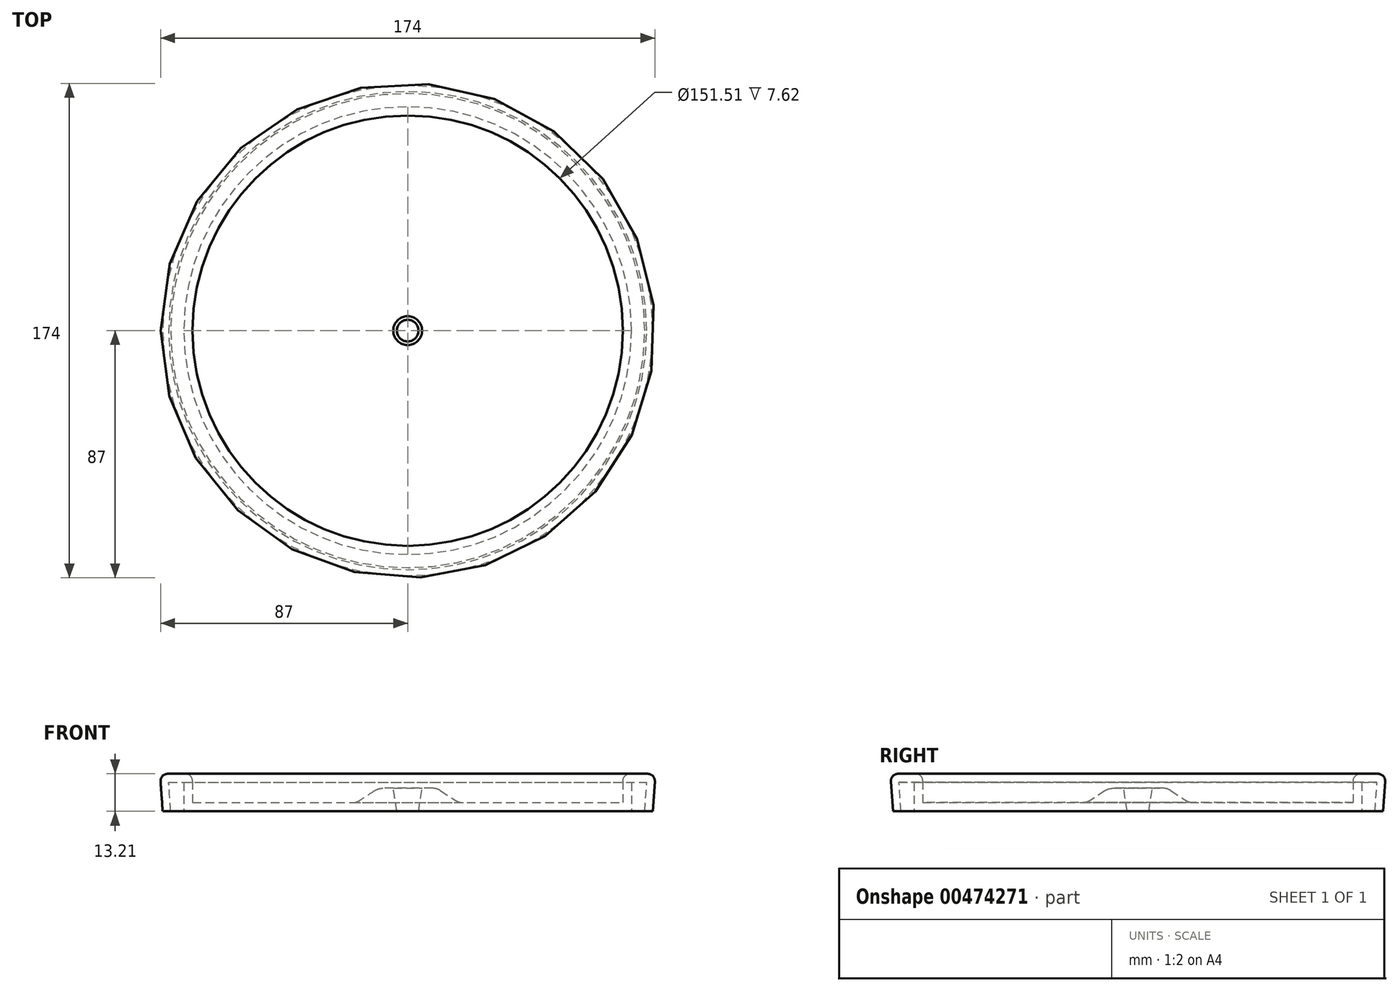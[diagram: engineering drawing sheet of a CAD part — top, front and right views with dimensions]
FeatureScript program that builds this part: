
annotation { "Feature Type Name" : "Feature", "Feature Type Description" : "" }
export const myFeature = defineFeature(function(context is Context, id is Id, definition is map)
    precondition{}
    {
        {
            var Q0;
            Q0=qCreatedBy(makeId("Front.planeOp"),FACE);
            var sketch = newSketch(context, id + "F0", { "sketchPlane" : qUnion([Q0])});
            skLineSegment(sketch, "E0", {"start": v(3.81, 0) * mm, "end": v(78.8, 0) * mm});
            skLineSegment(sketch, "E1", {"start": v(78.8, 0) * mm, "end": v(78.8, 10.16) * mm});
            skLineSegment(sketch, "E2", {"start": v(78.8, 10.16) * mm, "end": v(84.14, 10.16) * mm});
            skLineSegment(sketch, "E3.1", {"start": v(78.3, 13.2) * mm, "end": v(84.46, 13.2) * mm});
            skLineSegment(sketch, "E3.2", {"start": v(75.76, 3.05) * mm, "end": v(75.76, 10.67) * mm});
            skLineSegment(sketch, "E3.3", {"start": v(18.05, 3.05) * mm, "end": v(75.76, 3.05) * mm});
            skLineSegment(sketch, "E4", {"start": v(84.14, 10.16) * mm, "end": v(83.44, 0) * mm});
            skPoint(sketch, "E4.endSnap0", {"position": v(86.23, 0) * mm});
            skLineSegment(sketch, "E5", {"start": v(83.44, 0) * mm, "end": v(86.23, 0) * mm});
            skLineSegment(sketch, "E6", {"start": v(86.23, 0) * mm, "end": v(86.99, 10.49) * mm});
            skPoint(sketch, "E7.visualSharp", {"position": v(75.76, 13.2) * mm});
            skArc(sketch, "E7.filletArc", {"start": v(78.3, 13.2) * mm, "mid": v(76.5, 12.46) * mm, "end": v(75.76, 10.67) * mm});
            skPoint(sketch, "E8.visualSharp", {"position": v(87.19, 13.2) * mm});
            skArc(sketch, "E8.filletArc", {"start": v(86.99, 10.49) * mm, "mid": v(86.32, 12.4) * mm, "end": v(84.46, 13.2) * mm});
            skLineSegment(sketch, "E9", {"start": v(10.26, 8.13) * mm, "end": v(18.05, 3.05) * mm});
            skLineSegment(sketch, "E10", {"start": v(3.81, 0) * mm, "end": v(5.08, 8.13) * mm});
            skLineSegment(sketch, "E11", {"start": v(10.26, 8.13) * mm, "end": v(5.08, 8.13) * mm});
            skLineSegment(sketch, "E12", {"start": v(0, 0) * mm, "end": v(0, 5.08) * mm});
            skSolve(sketch);
        }
        {
            var Q0;
            Q0 = qSketchRegion(id + "F0", true);
            var Q1;
            Q1=sQuery(id+"F0.wireOp",EDGE,"E12");
            revolve(context, id + "F1", {"entities" : qUnion([Q0]), "axis" : qUnion([Q1]), "revolveType" : RevolveType.FULL});
        }
        {
            var Q0;
            Q0=makeQuery(id+"F1.opRevolve","SWEPT_EDGE",EDGE,{"disambiguationData":[OSD([sQuery(id+"F0.wireOp",EDGE,"E9"),sQuery(id+"F0.wireOp",EDGE,"E11")])]});
            var Q1;
            Q1=makeQuery(id+"F1.opRevolve","SWEPT_EDGE",EDGE,{"disambiguationData":[OSD([sQuery(id+"F0.wireOp",EDGE,"E3.3"),sQuery(id+"F0.wireOp",EDGE,"E9")])]});
            fillet(context, id + "F2", {"entities" : qUnion([Q0, Q1]), "radius" : 5.08 * mm, "tangentPropagation" : true, "allowEdgeOverflow" : false});
        }
    });
